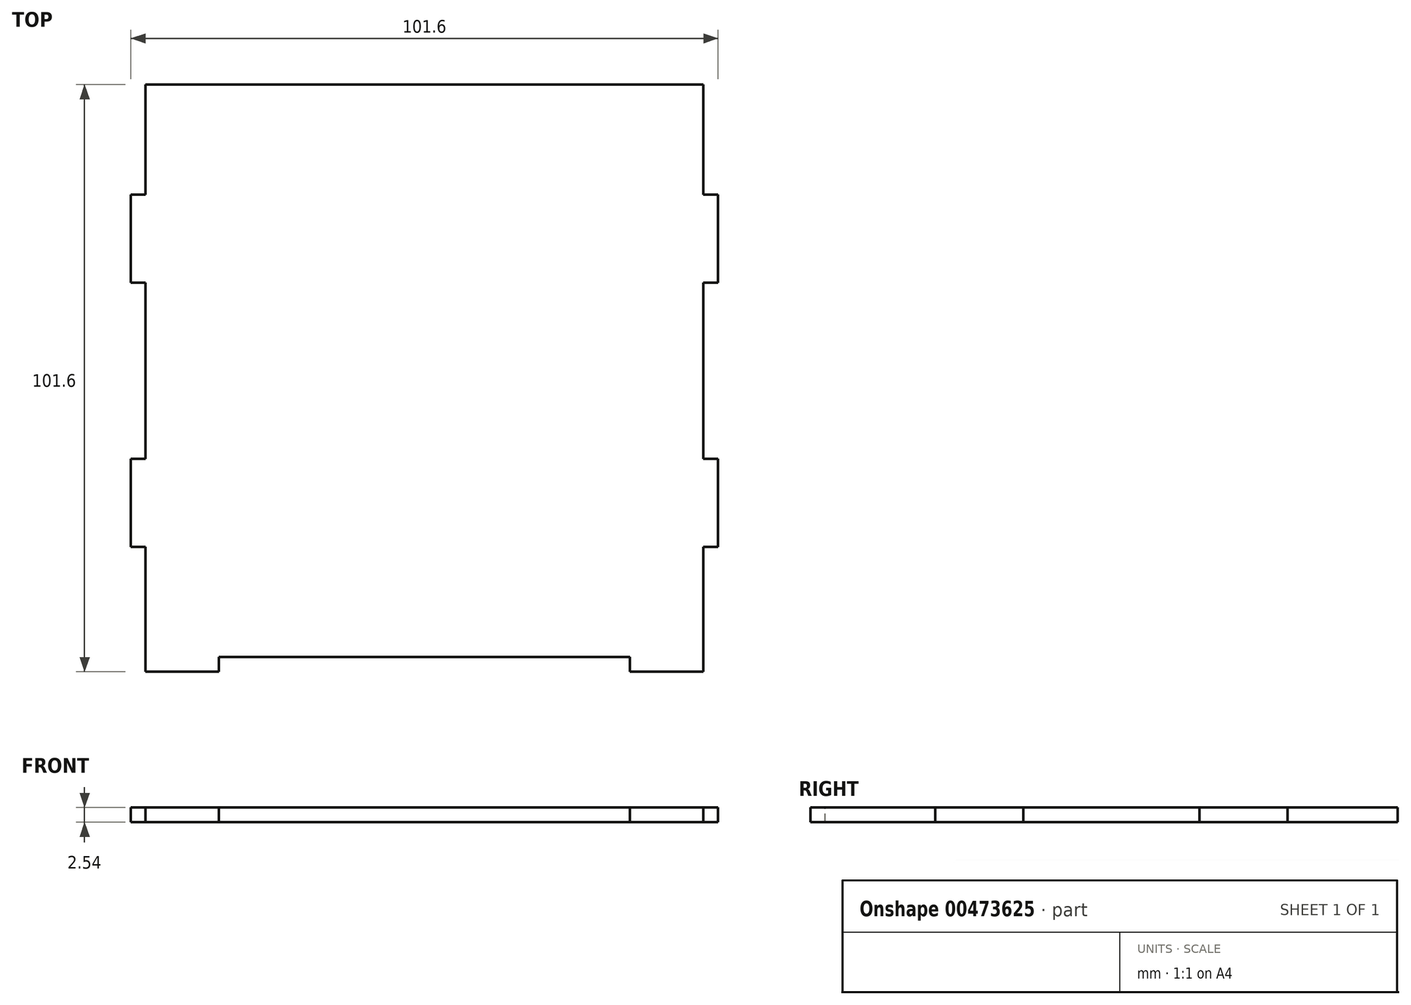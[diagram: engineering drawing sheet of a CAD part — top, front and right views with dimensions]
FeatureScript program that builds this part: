
annotation { "Feature Type Name" : "Feature", "Feature Type Description" : "" }
export const myFeature = defineFeature(function(context is Context, id is Id, definition is map)
    precondition{}
    {
        {
            var Q0;
            Q0=qCreatedBy(makeId("Top.planeOp"),FACE);
            var sketch = newSketch(context, id + "F0", { "sketchPlane" : qUnion([Q0])});
            skLineSegment(sketch, "E0.bottom", {"start": v(50.8, 50.8) * mm, "end": v(-50.8, 50.8) * mm});
            skLineSegment(sketch, "E0.top", {"start": v(50.8, -50.8) * mm, "end": v(-50.8, -50.8) * mm});
            skLineSegment(sketch, "E0.left", {"start": v(50.8, 50.8) * mm, "end": v(50.8, -50.8) * mm});
            skLineSegment(sketch, "E0.right", {"start": v(-50.8, 50.8) * mm, "end": v(-50.8, -50.8) * mm});
            skPoint(sketch, "E0.middle", {"position": v(0, 0) * mm});
            skSolve(sketch);
        }
        {
            var Q0;
            Q0=makeQuery(id+"F0.imprint","IMPRINT",FACE,{"disambiguationData":[TD([[makeQuery(id+"F0.imprint","IMPRINT",EDGE,{"derivedFrom":sQuery(id+"F0.wireOp",EDGE,"E0.bottom")}),1.0]])]});
            extrude(context, id + "F1", {"entities" : qUnion([Q0]), "depth" : 2.54 * mm});
        }
        {
            var Q0;
            Q0=makeQuery(id+"F1.opExtrude","SWEPT_FACE",FACE,{"disambiguationData":[OSD([sQuery(id+"F0.wireOp",EDGE,"E0.top")])]});
            var sketch = newSketch(context, id + "F2", { "sketchPlane" : qUnion([Q0])});
            skLineSegment(sketch, "E1", {"start": v(-39.37, 0) * mm, "end": v(-41.91, 2.54) * mm});
            skLineSegment(sketch, "E2", {"start": v(-41.91, 2.54) * mm, "end": v(41.9, 2.54) * mm});
            skLineSegment(sketch, "E3", {"start": v(41.9, 2.54) * mm, "end": v(39.37, 0) * mm});
            skLineSegment(sketch, "E4", {"start": v(39.37, 0) * mm, "end": v(-39.37, 0) * mm});
            skSolve(sketch);
        }
        {
            var Q0;
            Q0 = qSketchRegion(id + "F2", true);
            extrude(context, id + "F3", {"entities" : qUnion([Q0]), "operationType" : NewBodyOperationType.REMOVE, "oppositeDirection" : true, "depth" : 2.54 * mm});
        }
        {
            var Q0;
            Q0=makeQuery(id+"F1.opExtrude","CAP_FACE",FACE,{"disambiguationData":[OSD([sQuery(id+"F0.wireOp",EDGE,"E0.bottom"),sQuery(id+"F0.wireOp",EDGE,"E0.top"),sQuery(id+"F0.wireOp",EDGE,"E0.left"),sQuery(id+"F0.wireOp",EDGE,"E0.right")])],"isStart":false});
            var sketch = newSketch(context, id + "F4", { "sketchPlane" : qUnion([Q0])});
            skLineSegment(sketch, "E5", {"start": v(-50.8, -48.26) * mm, "end": v(-50.8, -31.75) * mm});
            skLineSegment(sketch, "E6", {"start": v(-50.8, -31.75) * mm, "end": v(-48.26, -31.75) * mm});
            skLineSegment(sketch, "E7", {"start": v(-48.26, -31.75) * mm, "end": v(-48.26, -48.26) * mm});
            skLineSegment(sketch, "E8", {"start": v(-48.26, -48.26) * mm, "end": v(-50.8, -48.26) * mm});
            skLineSegment(sketch, "E9", {"start": v(-50.8, -16.51) * mm, "end": v(-48.26, -16.51) * mm});
            skLineSegment(sketch, "E10", {"start": v(-48.26, -16.51) * mm, "end": v(-48.26, 13.97) * mm});
            skLineSegment(sketch, "E11", {"start": v(-48.26, 13.97) * mm, "end": v(-50.8, 13.97) * mm});
            skLineSegment(sketch, "E12", {"start": v(-50.8, 13.97) * mm, "end": v(-50.8, -16.51) * mm});
            skLineSegment(sketch, "E13", {"start": v(-50.8, 29.2) * mm, "end": v(-48.26, 29.2) * mm});
            skLineSegment(sketch, "E14", {"start": v(-48.26, 29.2) * mm, "end": v(-48.26, 50.8) * mm});
            skLineSegment(sketch, "E15", {"start": v(-48.26, 50.8) * mm, "end": v(-50.8, 50.8) * mm});
            skLineSegment(sketch, "E16", {"start": v(-50.8, 50.8) * mm, "end": v(-50.8, 29.2) * mm});
            skLineSegment(sketch, "E17", {"start": v(50.8, -48.26) * mm, "end": v(50.8, -31.75) * mm});
            skLineSegment(sketch, "E18", {"start": v(50.8, -31.75) * mm, "end": v(48.26, -31.75) * mm});
            skLineSegment(sketch, "E19", {"start": v(48.26, -31.75) * mm, "end": v(48.26, -48.26) * mm});
            skLineSegment(sketch, "E20", {"start": v(48.26, -48.26) * mm, "end": v(50.8, -48.26) * mm});
            skLineSegment(sketch, "E21", {"start": v(50.8, -16.5) * mm, "end": v(50.8, 13.97) * mm});
            skLineSegment(sketch, "E22", {"start": v(50.8, 13.97) * mm, "end": v(48.26, 13.97) * mm});
            skLineSegment(sketch, "E23", {"start": v(48.26, 13.97) * mm, "end": v(48.26, -16.5) * mm});
            skLineSegment(sketch, "E24", {"start": v(48.26, -16.5) * mm, "end": v(50.8, -16.5) * mm});
            skLineSegment(sketch, "E25", {"start": v(50.8, 29.21) * mm, "end": v(48.26, 29.21) * mm});
            skLineSegment(sketch, "E26", {"start": v(48.26, 29.21) * mm, "end": v(48.26, 50.8) * mm});
            skLineSegment(sketch, "E27", {"start": v(48.26, 50.8) * mm, "end": v(50.8, 50.8) * mm});
            skLineSegment(sketch, "E28", {"start": v(50.8, 50.8) * mm, "end": v(50.8, 29.21) * mm});
            skSolve(sketch);
        }
        {
            var Q0;
            Q0 = qSketchRegion(id + "F4", true);
            extrude(context, id + "F5", {"entities" : qUnion([Q0]), "operationType" : NewBodyOperationType.REMOVE, "oppositeDirection" : true, "depth" : 25.4 * mm});
        }
        {
            var Q0;
            Q0=makeQuery(id+"F1.opExtrude","CAP_FACE",FACE,{"disambiguationData":[OSD([sQuery(id+"F0.wireOp",EDGE,"E0.bottom"),sQuery(id+"F0.wireOp",EDGE,"E0.top"),sQuery(id+"F0.wireOp",EDGE,"E0.left"),sQuery(id+"F0.wireOp",EDGE,"E0.right")])],"isStart":false});
            var sketch = newSketch(context, id + "F6", { "sketchPlane" : qUnion([Q0])});
            skLineSegment(sketch, "E29.bottom", {"start": v(48.26, -48.26) * mm, "end": v(56.4, -48.26) * mm});
            skLineSegment(sketch, "E29.top", {"start": v(48.26, -54.68) * mm, "end": v(56.4, -54.68) * mm});
            skLineSegment(sketch, "E29.left", {"start": v(48.26, -48.26) * mm, "end": v(48.26, -54.68) * mm});
            skLineSegment(sketch, "E29.right", {"start": v(56.4, -48.26) * mm, "end": v(56.4, -54.68) * mm});
            skPoint(sketch, "E30.oppositeSnap0", {"position": v(52.33, -54.68) * mm});
            skLineSegment(sketch, "E30.bottom", {"start": v(-48.26, -48.26) * mm, "end": v(-54.97, -48.26) * mm});
            skLineSegment(sketch, "E30.top", {"start": v(-48.26, -54.68) * mm, "end": v(-54.97, -54.68) * mm});
            skLineSegment(sketch, "E30.left", {"start": v(-48.26, -48.26) * mm, "end": v(-48.26, -54.68) * mm});
            skLineSegment(sketch, "E30.right", {"start": v(-54.97, -48.26) * mm, "end": v(-54.97, -54.68) * mm});
            skSolve(sketch);
        }
        {
            var Q0;
            Q0 = qSketchRegion(id + "F6", true);
            extrude(context, id + "F7", {"entities" : qUnion([Q0]), "operationType" : NewBodyOperationType.REMOVE, "oppositeDirection" : true, "depth" : 25.4 * mm});
        }
        {
            var Q0;
            Q0=makeQuery(id+"F1.opExtrude","CAP_FACE",FACE,{"disambiguationData":[OSD([sQuery(id+"F0.wireOp",EDGE,"E0.bottom"),sQuery(id+"F0.wireOp",EDGE,"E0.top"),sQuery(id+"F0.wireOp",EDGE,"E0.left"),sQuery(id+"F0.wireOp",EDGE,"E0.right")])],"isStart":false});
            var sketch = newSketch(context, id + "F8", { "sketchPlane" : qUnion([Q0])});
            skLineSegment(sketch, "E31", {"start": v(35.56, -48.26) * mm, "end": v(35.56, -50.8) * mm});
            skLineSegment(sketch, "E32", {"start": v(35.56, -50.8) * mm, "end": v(48.26, -50.8) * mm});
            skLineSegment(sketch, "E33", {"start": v(48.26, -50.8) * mm, "end": v(48.26, -48.26) * mm});
            skLineSegment(sketch, "E34", {"start": v(48.26, -48.26) * mm, "end": v(35.56, -48.26) * mm});
            skLineSegment(sketch, "E35", {"start": v(-48.26, -50.8) * mm, "end": v(-35.56, -50.8) * mm});
            skPoint(sketch, "E35.endSnap0", {"position": v(-45.09, -50.8) * mm});
            skLineSegment(sketch, "E36", {"start": v(-35.56, -50.8) * mm, "end": v(-35.56, -48.26) * mm});
            skLineSegment(sketch, "E37", {"start": v(-35.56, -48.26) * mm, "end": v(-48.26, -48.26) * mm});
            skLineSegment(sketch, "E38", {"start": v(-48.26, -48.26) * mm, "end": v(-48.26, -50.8) * mm});
            skSolve(sketch);
        }
        {
            var Q0;
            Q0 = qSketchRegion(id + "F8", true);
            extrude(context, id + "F9", {"entities" : qUnion([Q0]), "operationType" : NewBodyOperationType.ADD, "oppositeDirection" : true, "depth" : 2.54 * mm, "offsetDistance" : 25.4 * mm});
        }
        {
            var Q0;
            Q0=makeQuery(id+"F9.boolean.opBoolean","MERGE",FACE,{"derivedFrom":[makeQuery(id+"F1.opExtrude","CAP_FACE",FACE,{"disambiguationData":[OSD([sQuery(id+"F0.wireOp",EDGE,"E0.bottom"),sQuery(id+"F0.wireOp",EDGE,"E0.top"),sQuery(id+"F0.wireOp",EDGE,"E0.left"),sQuery(id+"F0.wireOp",EDGE,"E0.right")])],"isStart":false}),makeQuery(id+"F9.opExtrude","CAP_FACE",FACE,{"disambiguationData":[OSD([sQuery(id+"F8.wireOp",EDGE,"E31"),sQuery(id+"F8.wireOp",EDGE,"E32"),sQuery(id+"F8.wireOp",EDGE,"E33"),sQuery(id+"F8.wireOp",EDGE,"E34")])],"isStart":true}),makeQuery(id+"F9.opExtrude","CAP_FACE",FACE,{"disambiguationData":[OSD([sQuery(id+"F8.wireOp",EDGE,"E35"),sQuery(id+"F8.wireOp",EDGE,"E36"),sQuery(id+"F8.wireOp",EDGE,"E37"),sQuery(id+"F8.wireOp",EDGE,"E38")])],"isStart":true})]});
            var sketch = newSketch(context, id + "F10", { "sketchPlane" : qUnion([Q0])});
            skLineSegment(sketch, "E39", {"start": v(-50.8, 29.2) * mm, "end": v(-50.8, 31.75) * mm});
            skLineSegment(sketch, "E40", {"start": v(-50.8, 31.75) * mm, "end": v(-48.26, 31.75) * mm});
            skLineSegment(sketch, "E41", {"start": v(-48.26, 31.75) * mm, "end": v(-48.26, 29.2) * mm});
            skLineSegment(sketch, "E42", {"start": v(-48.26, 29.2) * mm, "end": v(-50.8, 29.2) * mm});
            skLineSegment(sketch, "E43", {"start": v(-50.8, -16.51) * mm, "end": v(-50.8, -13.97) * mm});
            skLineSegment(sketch, "E44", {"start": v(-50.8, -13.97) * mm, "end": v(-48.26, -13.97) * mm});
            skLineSegment(sketch, "E45", {"start": v(-48.26, -13.97) * mm, "end": v(-48.26, -16.51) * mm});
            skLineSegment(sketch, "E46", {"start": v(-48.26, -16.51) * mm, "end": v(-50.8, -16.51) * mm});
            skLineSegment(sketch, "E47", {"start": v(48.26, -16.5) * mm, "end": v(48.26, -13.97) * mm});
            skLineSegment(sketch, "E48", {"start": v(48.26, -13.97) * mm, "end": v(50.8, -13.97) * mm});
            skLineSegment(sketch, "E49", {"start": v(50.8, -13.97) * mm, "end": v(50.8, -16.5) * mm});
            skLineSegment(sketch, "E50", {"start": v(50.8, -16.5) * mm, "end": v(48.26, -16.5) * mm});
            skLineSegment(sketch, "E51", {"start": v(48.26, 29.21) * mm, "end": v(48.26, 31.75) * mm});
            skLineSegment(sketch, "E52", {"start": v(48.26, 31.75) * mm, "end": v(50.8, 31.75) * mm});
            skLineSegment(sketch, "E53", {"start": v(50.8, 31.75) * mm, "end": v(50.8, 29.21) * mm});
            skLineSegment(sketch, "E54", {"start": v(50.8, 29.21) * mm, "end": v(48.26, 29.21) * mm});
            skSolve(sketch);
        }
        {
            var Q0;
            Q0 = qSketchRegion(id + "F10", true);
            extrude(context, id + "F11", {"entities" : qUnion([Q0]), "operationType" : NewBodyOperationType.ADD, "oppositeDirection" : true, "depth" : 2.54 * mm, "offsetDistance" : 25.4 * mm});
        }
        {
            var Q0;
            Q0=makeQuery(id+"F11.boolean.opBoolean","MERGE",FACE,{"derivedFrom":[makeQuery(id+"F9.boolean.opBoolean","MERGE",FACE,{"derivedFrom":[makeQuery(id+"F1.opExtrude","CAP_FACE",FACE,{"disambiguationData":[OSD([sQuery(id+"F0.wireOp",EDGE,"E0.bottom"),sQuery(id+"F0.wireOp",EDGE,"E0.top"),sQuery(id+"F0.wireOp",EDGE,"E0.left"),sQuery(id+"F0.wireOp",EDGE,"E0.right")])],"isStart":false}),makeQuery(id+"F9.opExtrude","CAP_FACE",FACE,{"disambiguationData":[OSD([sQuery(id+"F8.wireOp",EDGE,"E31"),sQuery(id+"F8.wireOp",EDGE,"E32"),sQuery(id+"F8.wireOp",EDGE,"E33"),sQuery(id+"F8.wireOp",EDGE,"E34")])],"isStart":true}),makeQuery(id+"F9.opExtrude","CAP_FACE",FACE,{"disambiguationData":[OSD([sQuery(id+"F8.wireOp",EDGE,"E35"),sQuery(id+"F8.wireOp",EDGE,"E36"),sQuery(id+"F8.wireOp",EDGE,"E37"),sQuery(id+"F8.wireOp",EDGE,"E38")])],"isStart":true})]}),makeQuery(id+"F11.opExtrude","CAP_FACE",FACE,{"disambiguationData":[OSD([sQuery(id+"F10.wireOp",EDGE,"E39"),sQuery(id+"F10.wireOp",EDGE,"E40"),sQuery(id+"F10.wireOp",EDGE,"E41"),sQuery(id+"F10.wireOp",EDGE,"E42")])],"isStart":true}),makeQuery(id+"F11.opExtrude","CAP_FACE",FACE,{"disambiguationData":[OSD([sQuery(id+"F10.wireOp",EDGE,"E43"),sQuery(id+"F10.wireOp",EDGE,"E44"),sQuery(id+"F10.wireOp",EDGE,"E45"),sQuery(id+"F10.wireOp",EDGE,"E46")])],"isStart":true}),makeQuery(id+"F11.opExtrude","CAP_FACE",FACE,{"disambiguationData":[OSD([sQuery(id+"F10.wireOp",EDGE,"E47"),sQuery(id+"F10.wireOp",EDGE,"E48"),sQuery(id+"F10.wireOp",EDGE,"E49"),sQuery(id+"F10.wireOp",EDGE,"E50")])],"isStart":true}),makeQuery(id+"F11.opExtrude","CAP_FACE",FACE,{"disambiguationData":[OSD([sQuery(id+"F10.wireOp",EDGE,"E51"),sQuery(id+"F10.wireOp",EDGE,"E52"),sQuery(id+"F10.wireOp",EDGE,"E53"),sQuery(id+"F10.wireOp",EDGE,"E54")])],"isStart":true})]});
            var sketch = newSketch(context, id + "F12", { "sketchPlane" : qUnion([Q0])});
            skLineSegment(sketch, "E55.bottom", {"start": v(48.26, -31.75) * mm, "end": v(50.8, -31.75) * mm});
            skLineSegment(sketch, "E55.top", {"start": v(48.26, -29.2) * mm, "end": v(50.8, -29.2) * mm});
            skLineSegment(sketch, "E55.left", {"start": v(48.26, -31.75) * mm, "end": v(48.26, -29.2) * mm});
            skLineSegment(sketch, "E55.right", {"start": v(50.8, -31.75) * mm, "end": v(50.8, -29.2) * mm});
            skLineSegment(sketch, "E56.bottom", {"start": v(48.26, 13.97) * mm, "end": v(50.8, 13.97) * mm});
            skLineSegment(sketch, "E56.top", {"start": v(48.26, 16.51) * mm, "end": v(50.8, 16.51) * mm});
            skLineSegment(sketch, "E56.left", {"start": v(48.26, 13.97) * mm, "end": v(48.26, 16.51) * mm});
            skLineSegment(sketch, "E56.right", {"start": v(50.8, 13.97) * mm, "end": v(50.8, 16.51) * mm});
            skLineSegment(sketch, "E57.bottom", {"start": v(-48.26, -31.75) * mm, "end": v(-50.8, -31.75) * mm});
            skLineSegment(sketch, "E57.top", {"start": v(-48.26, -29.2) * mm, "end": v(-50.8, -29.2) * mm});
            skLineSegment(sketch, "E57.left", {"start": v(-48.26, -31.75) * mm, "end": v(-48.26, -29.2) * mm});
            skLineSegment(sketch, "E57.right", {"start": v(-50.8, -31.75) * mm, "end": v(-50.8, -29.2) * mm});
            skLineSegment(sketch, "E58.bottom", {"start": v(-48.26, 13.97) * mm, "end": v(-50.8, 13.97) * mm});
            skLineSegment(sketch, "E58.top", {"start": v(-48.26, 16.5) * mm, "end": v(-50.8, 16.5) * mm});
            skLineSegment(sketch, "E58.left", {"start": v(-48.26, 13.97) * mm, "end": v(-48.26, 16.5) * mm});
            skLineSegment(sketch, "E58.right", {"start": v(-50.8, 13.97) * mm, "end": v(-50.8, 16.5) * mm});
            skSolve(sketch);
        }
        {
            var Q0;
            Q0 = qSketchRegion(id + "F12", true);
            extrude(context, id + "F13", {"entities" : qUnion([Q0]), "operationType" : NewBodyOperationType.REMOVE, "oppositeDirection" : true, "depth" : 25.4 * mm, "offsetDistance" : 25.4 * mm});
        }
    });
